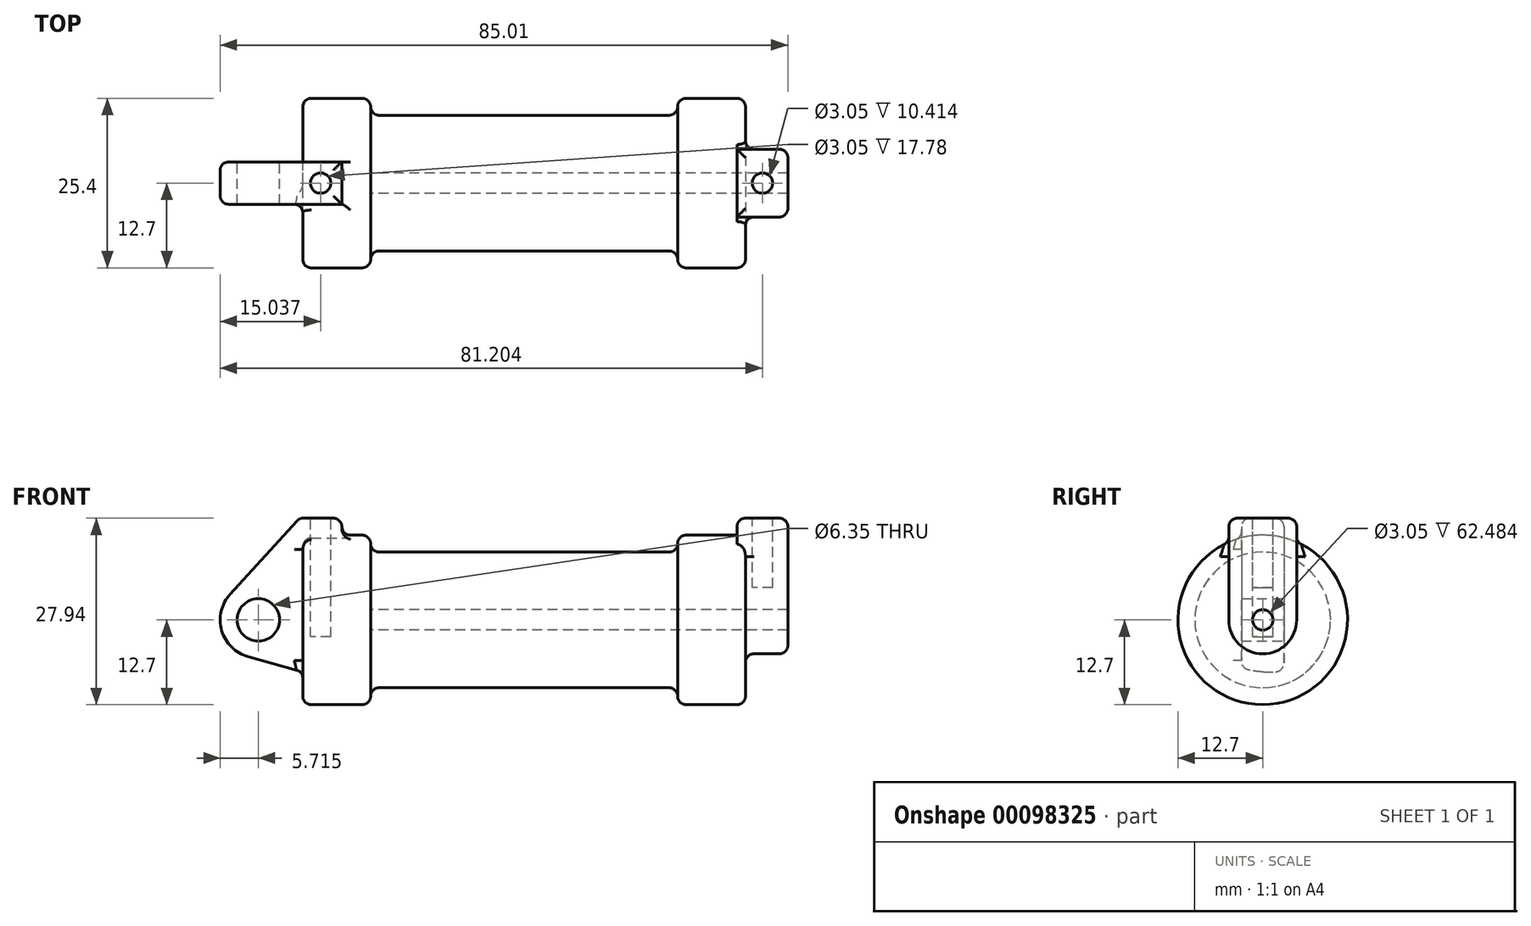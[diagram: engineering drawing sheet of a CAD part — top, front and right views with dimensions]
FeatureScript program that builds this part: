
annotation { "Feature Type Name" : "Feature", "Feature Type Description" : "" }
export const myFeature = defineFeature(function(context is Context, id is Id, definition is map)
    precondition{}
    {
        {
            var Q0;
            Q0=qCreatedBy(makeId("Front.planeOp"),FACE);
            var sketch = newSketch(context, id + "F0", { "sketchPlane" : qUnion([Q0])});
            skLineSegment(sketch, "E0", {"start": v(0, 0) * mm, "end": v(0, 12.7) * mm});
            skLineSegment(sketch, "E1", {"start": v(0, 12.7) * mm, "end": v(10.16, 12.7) * mm});
            skLineSegment(sketch, "E2", {"start": v(10.16, 12.7) * mm, "end": v(10.16, 10.16) * mm});
            skLineSegment(sketch, "E3", {"start": v(10.16, 10.16) * mm, "end": v(56.13, 10.16) * mm});
            skLineSegment(sketch, "E4", {"start": v(56.13, 10.16) * mm, "end": v(56.13, 12.7) * mm});
            skLineSegment(sketch, "E5", {"start": v(56.13, 12.7) * mm, "end": v(66.3, 12.7) * mm});
            skLineSegment(sketch, "E6", {"start": v(66.3, 12.7) * mm, "end": v(66.3, 0) * mm});
            skLineSegment(sketch, "E7", {"start": v(66.3, 0) * mm, "end": v(0, 0) * mm});
            skLineSegment(sketch, "E8", {"start": v(5.84, 15.24) * mm, "end": v(-0.5, 15.24) * mm});
            skLineSegment(sketch, "E9", {"start": v(-0.5, 15.24) * mm, "end": v(-10.88, 3.85) * mm});
            skLineSegment(sketch, "E10", {"start": v(0, 0) * mm, "end": v(-6.65, 0) * mm});
            skCircle(sketch, "E11", {"center": v(-6.65, 0) * mm, "radius": 5.72 * mm});
            skCircle(sketch, "E12", {"center": v(-6.65, 0) * mm, "radius": 3.18 * mm});
            skLineSegment(sketch, "E13", {"start": v(5.84, 15.24) * mm, "end": v(5.84, -9.4) * mm});
            skLineSegment(sketch, "E14", {"start": v(5.84, -9.4) * mm, "end": v(-8.18, -5.5) * mm});
            skSolve(sketch);
        }
        {
            var Q0;
            {var subQ0=sQuery(id+"F0.wireOp",EDGE,"E2");Q0=makeQuery(id+"F0.imprint","IMPRINT",FACE,{"disambiguationData":[TD([[makeQuery(id+"F0.imprint","IMPRINT",EDGE,{"derivedFrom":subQ0}),-1.0]])]});}
            var Q1;
            {var subQ0=sQuery(id+"F0.wireOp",EDGE,"E0");Q1=makeQuery(id+"F0.imprint","IMPRINT",FACE,{"disambiguationData":[TD([[makeQuery(id+"F0.imprint","IMPRINT",EDGE,{"derivedFrom":subQ0}),-1.0]])]});}
            var Q2;
            Q2=sQuery(id+"F0.wireOp",EDGE,"E10");
            revolve(context, id + "F1", {"entities" : qUnion([Q0, Q1]), "axis" : qUnion([Q2]), "revolveType" : RevolveType.FULL});
        }
        {
            var Q0;
            {var subQ3=sQuery(id+"F0.wireOp",EDGE,"E0");Q0=makeQuery(id+"F0.imprint","IMPRINT",FACE,{"disambiguationData":[TD([[makeQuery(id+"F0.imprint","IMPRINT",EDGE,{"derivedFrom":subQ3}),1.0]])]});}
            var Q1;
            {var subQ0=sQuery(id+"F0.wireOp",EDGE,"E14");Q1=makeQuery(id+"F0.imprint","IMPRINT",FACE,{"disambiguationData":[TD([[makeQuery(id+"F0.imprint","IMPRINT",EDGE,{"derivedFrom":subQ0}),-1.0]])]});}
            var Q2;
            {var subQ4=sQuery(id+"F0.wireOp",EDGE,"E12");Q2=makeQuery(id+"F0.imprint","IMPRINT",FACE,{"disambiguationData":[TD([[makeQuery(id+"F0.imprint","IMPRINT",EDGE,{"derivedFrom":subQ4}),-1.0]])]});}
            var Q3;
            {var subQ0=sQuery(id+"F0.wireOp",EDGE,"E0");Q3=makeQuery(id+"F0.imprint","IMPRINT",FACE,{"disambiguationData":[TD([[makeQuery(id+"F0.imprint","IMPRINT",EDGE,{"derivedFrom":subQ0}),-1.0]])]});}
            extrude(context, id + "F2", {"entities" : qUnion([Q0, Q1, Q2, Q3]), "operationType" : NewBodyOperationType.ADD, "endBound" : BoundingType.SYMMETRIC, "depth" : 6.35 * mm});
        }
        {
            var Q0;
            Q0=makeQuery(id+"F1.opRevolve","SWEPT_FACE",FACE,{"disambiguationData":[OSD([sQuery(id+"F0.wireOp",EDGE,"E6")])]});
            var sketch = newSketch(context, id + "F3", { "sketchPlane" : qUnion([Q0])});
            skCircle(sketch, "E15", {"center": v(0, 0) * mm, "radius": 1.52 * mm});
            skCircle(sketch, "E16", {"center": v(0, 0) * mm, "radius": 5.08 * mm});
            skLineSegment(sketch, "E17", {"start": v(5.08, 0) * mm, "end": v(5.08, 15.24) * mm});
            skLineSegment(sketch, "E18", {"start": v(5.08, 15.24) * mm, "end": v(-5.08, 15.24) * mm});
            skLineSegment(sketch, "E19", {"start": v(-5.08, 15.24) * mm, "end": v(-5.08, 0) * mm});
            skSolve(sketch);
        }
        {
            var Q0;
            Q0=makeQuery(id+"F3.imprint","IMPRINT",FACE,{"disambiguationData":[TD([[makeQuery(id+"F3.imprint","IMPRINT",EDGE,{"derivedFrom":sQuery(id+"F3.wireOp",EDGE,"E15")}),-1.0]])]});
            var Q1;
            {var subQ0=sQuery(id+"F3.wireOp",EDGE,"E17");var subQ1=sQuery(id+"F3.wireOp",EDGE,"E16");var subQ2=makeQuery(id+"F3.imprint","INTERSECT",VERTEX,{"derivedFrom":[subQ1,subQ0]});Q1=makeQuery(id+"F3.imprint","IMPRINT",FACE,{"disambiguationData":[TD([[makeQuery(id+"F3.imprint","IMPRINT",EDGE,{"disambiguationData":[TD([[subQ2,-1.0]])],"derivedFrom":subQ1}),-1.0]])]});}
            var Q2;
            {var subQ0=sQuery(id+"F3.wireOp",EDGE,"E18");Q2=makeQuery(id+"F3.imprint","IMPRINT",FACE,{"disambiguationData":[TD([[makeQuery(id+"F3.imprint","IMPRINT",EDGE,{"derivedFrom":subQ0}),1.0]])]});}
            extrude(context, id + "F4", {"entities" : qUnion([Q0, Q1, Q2]), "operationType" : NewBodyOperationType.ADD, "depth" : 6.35 * mm});
        }
        {
            var Q0;
            {var subQ0=sQuery(id+"F3.wireOp",EDGE,"E18");Q0=makeQuery(id+"F3.imprint","IMPRINT",FACE,{"disambiguationData":[TD([[makeQuery(id+"F3.imprint","IMPRINT",EDGE,{"derivedFrom":subQ0}),1.0]])]});}
            var Q1;
            Q1=makeQuery(id+"F3.imprint","IMPRINT",FACE,{"disambiguationData":[TD([[makeQuery(id+"F3.imprint","IMPRINT",EDGE,{"derivedFrom":sQuery(id+"F3.wireOp",EDGE,"E15")}),1.0]])]});
            extrude(context, id + "F5", {"entities" : qUnion([Q0, Q1]), "operationType" : NewBodyOperationType.ADD, "oppositeDirection" : true, "depth" : 1.27 * mm});
        }
        {
            var Q0;
            Q0=makeQuery(id+"F3.imprint","IMPRINT",FACE,{"disambiguationData":[TD([[makeQuery(id+"F3.imprint","IMPRINT",EDGE,{"derivedFrom":sQuery(id+"F3.wireOp",EDGE,"E15")}),1.0]])]});
            var Q1;
            Q1=makeQuery(id+"F1.opRevolve","SWEPT_FACE",FACE,{"disambiguationData":[OSD([sQuery(id+"F0.wireOp",EDGE,"E2")])]});
            extrude(context, id + "F6", {"entities" : qUnion([Q0]), "operationType" : NewBodyOperationType.REMOVE, "endBound" : BoundingType.UP_TO_SURFACE, "oppositeDirection" : true, "endBoundEntityFace" : qUnion([Q1]), "depth" : 25.4 * mm});
        }
        {
            var Q0;
            {var subQ0=sQuery(id+"F3.wireOp",EDGE,"E18");Q0=makeQuery(id+"F5.boolean.opBoolean","MERGE",FACE,{"derivedFrom":[makeQuery(id+"F4.opExtrude","SWEPT_FACE",FACE,{"disambiguationData":[OSD([subQ0])]}),makeQuery(id+"F5.opExtrude","SWEPT_FACE",FACE,{"disambiguationData":[OSD([subQ0])]})]});}
            var sketch = newSketch(context, id + "F7", { "sketchPlane" : qUnion([Q0])});
            skCircle(sketch, "E20", {"center": v(2.67, 0) * mm, "radius": 1.52 * mm});
            skLineSegment(sketch, "E21", {"start": v(-0.5, 0) * mm, "end": v(5.84, 0) * mm, "construction": true});
            skLineSegment(sketch, "E22", {"start": v(65.02, 0) * mm, "end": v(72.64, 0) * mm, "construction": true});
            skCircle(sketch, "E23", {"center": v(68.83, 0) * mm, "radius": 1.52 * mm});
            skSolve(sketch);
        }
        {
            var Q0;
            Q0=makeQuery(id+"F7.imprint","IMPRINT",FACE,{"disambiguationData":[TD([[makeQuery(id+"F7.imprint","IMPRINT",EDGE,{"derivedFrom":sQuery(id+"F7.wireOp",EDGE,"E23")}),1.0]])]});
            extrude(context, id + "F8", {"entities" : qUnion([Q0]), "operationType" : NewBodyOperationType.REMOVE, "oppositeDirection" : true, "depth" : 10.4 * mm});
        }
        {
            var Q0;
            Q0=makeQuery(id+"F7.imprint","IMPRINT",FACE,{"disambiguationData":[TD([[makeQuery(id+"F7.imprint","IMPRINT",EDGE,{"derivedFrom":sQuery(id+"F7.wireOp",EDGE,"E20")}),1.0]])]});
            extrude(context, id + "F9", {"entities" : qUnion([Q0]), "operationType" : NewBodyOperationType.REMOVE, "oppositeDirection" : true, "depth" : 17.78 * mm});
        }
        {
            var Q0;
            Q0=makeQuery(id+"F1.opRevolve","SWEPT_EDGE",EDGE,{"disambiguationData":[OSD([sQuery(id+"F0.wireOp",EDGE,"E1"),sQuery(id+"F0.wireOp",EDGE,"E2")])]});
            var Q1;
            Q1=makeQuery(id+"F1.opRevolve","SWEPT_EDGE",EDGE,{"disambiguationData":[OSD([sQuery(id+"F0.wireOp",EDGE,"E2"),sQuery(id+"F0.wireOp",EDGE,"E3")])]});
            var Q2;
            Q2=makeQuery(id+"F1.opRevolve","SWEPT_EDGE",EDGE,{"disambiguationData":[OSD([sQuery(id+"F0.wireOp",EDGE,"E4"),sQuery(id+"F0.wireOp",EDGE,"E5")])]});
            var Q3;
            Q3=makeQuery(id+"F4.boolean.opBoolean","SPLIT",EDGE,{"disambiguationData":[OD(1.0)],"derivedFrom":makeQuery(id+"F1.opRevolve","SWEPT_EDGE",EDGE,{"disambiguationData":[OSD([sQuery(id+"F0.wireOp",EDGE,"E5"),sQuery(id+"F0.wireOp",EDGE,"E6")])]})});
            var Q4;
            Q4=makeQuery(id+"F1.opRevolve","SWEPT_EDGE",EDGE,{"disambiguationData":[OSD([sQuery(id+"F0.wireOp",EDGE,"E0"),sQuery(id+"F0.wireOp",EDGE,"E1")])]});
            var Q5;
            Q5=makeQuery(id+"F1.opRevolve","SWEPT_EDGE",EDGE,{"disambiguationData":[OSD([sQuery(id+"F0.wireOp",EDGE,"E3"),sQuery(id+"F0.wireOp",EDGE,"E4")])]});
            fillet(context, id + "F10", {"entities" : qUnion([Q0, Q1, Q2, Q3, Q4, Q5]), "radius" : 1.27 * mm, "tangentPropagation" : true, "allowEdgeOverflow" : false});
        }
        {
            var Q0;
            Q0=makeQuery(id+"F2.opExtrude","CAP_EDGE",EDGE,{"disambiguationData":[OSD([sQuery(id+"F0.wireOp",EDGE,"E8")])],"isStart":false});
            var Q1;
            Q1=makeQuery(id+"F2.opExtrude","SWEPT_EDGE",EDGE,{"disambiguationData":[OSD([sQuery(id+"F0.wireOp",EDGE,"E8"),sQuery(id+"F0.wireOp",EDGE,"E13")])]});
            var Q2;
            Q2=makeQuery(id+"F2.opExtrude","CAP_EDGE",EDGE,{"disambiguationData":[OSD([sQuery(id+"F0.wireOp",EDGE,"E8")])],"isStart":true});
            var Q3;
            Q3=makeQuery(id+"F2.opExtrude","SWEPT_EDGE",EDGE,{"disambiguationData":[OSD([sQuery(id+"F0.wireOp",EDGE,"E8"),sQuery(id+"F0.wireOp",EDGE,"E9")])]});
            var Q4;
            Q4=makeQuery(id+"F2.opExtrude","CAP_EDGE",EDGE,{"disambiguationData":[OSD([sQuery(id+"F0.wireOp",EDGE,"E9")])],"isStart":true});
            var Q5;
            Q5=makeQuery(id+"F2.opExtrude","CAP_EDGE",EDGE,{"disambiguationData":[OSD([sQuery(id+"F0.wireOp",EDGE,"E9")])],"isStart":false});
            var Q6;
            Q6=makeQuery(id+"F2.boolean.opBoolean","INTERSECT",EDGE,{"derivedFrom":[makeQuery(id+"F1.opRevolve","SWEPT_FACE",FACE,{"disambiguationData":[OSD([sQuery(id+"F0.wireOp",EDGE,"E1")])]}),makeQuery(id+"F2.opExtrude","CAP_FACE",FACE,{"disambiguationData":[OSD([sQuery(id+"F0.wireOp",EDGE,"E8"),sQuery(id+"F0.wireOp",EDGE,"E9"),sQuery(id+"F0.wireOp",EDGE,"E11"),sQuery(id+"F0.wireOp",EDGE,"E12"),sQuery(id+"F0.wireOp",EDGE,"E13"),sQuery(id+"F0.wireOp",EDGE,"E14")])],"isStart":false})]});
            var Q7;
            Q7=makeQuery(id+"F2.boolean.opBoolean","INTERSECT",EDGE,{"derivedFrom":[makeQuery(id+"F1.opRevolve","SWEPT_FACE",FACE,{"disambiguationData":[OSD([sQuery(id+"F0.wireOp",EDGE,"E1")])]}),makeQuery(id+"F2.opExtrude","SWEPT_FACE",FACE,{"disambiguationData":[OSD([sQuery(id+"F0.wireOp",EDGE,"E13")])]})]});
            fillet(context, id + "F11", {"entities" : qUnion([Q0, Q1, Q2, Q3, Q4, Q5, Q6, Q7]), "radius" : 1.27 * mm, "tangentPropagation" : true, "allowEdgeOverflow" : false});
        }
        {
            var Q0;
            {var subQ0=sQuery(id+"F3.wireOp",EDGE,"E19");var subQ1=sQuery(id+"F3.wireOp",EDGE,"E18");Q0=makeQuery(id+"F5.boolean.opBoolean","MERGE",EDGE,{"derivedFrom":[makeQuery(id+"F4.opExtrude","SWEPT_EDGE",EDGE,{"disambiguationData":[OSD([subQ1,subQ0])]}),makeQuery(id+"F5.opExtrude","SWEPT_EDGE",EDGE,{"disambiguationData":[OSD([subQ1,subQ0])]})]});}
            var Q1;
            Q1=makeQuery(id+"F4.opExtrude","CAP_EDGE",EDGE,{"disambiguationData":[OSD([sQuery(id+"F3.wireOp",EDGE,"E18")])],"isStart":false});
            var Q2;
            {var subQ0=sQuery(id+"F3.wireOp",EDGE,"E18");var subQ1=sQuery(id+"F3.wireOp",EDGE,"E17");Q2=makeQuery(id+"F5.boolean.opBoolean","MERGE",EDGE,{"derivedFrom":[makeQuery(id+"F4.opExtrude","SWEPT_EDGE",EDGE,{"disambiguationData":[OSD([subQ1,subQ0])]}),makeQuery(id+"F5.opExtrude","SWEPT_EDGE",EDGE,{"disambiguationData":[OSD([subQ1,subQ0])]})]});}
            var Q3;
            Q3=makeQuery(id+"F5.opExtrude","CAP_EDGE",EDGE,{"disambiguationData":[OSD([sQuery(id+"F3.wireOp",EDGE,"E18")])],"isStart":false});
            var Q4;
            {var subQ0=sQuery(id+"F3.wireOp",EDGE,"E19");var subQ1=sQuery(id+"F3.wireOp",EDGE,"E16");Q4=makeQuery(id+"F4.boolean.opBoolean","SPLIT",EDGE,{"disambiguationData":[TD([makeQuery(id+"F4.opExtrude","SWEPT_FACE",FACE,{"disambiguationData":[OSD([subQ1])]})])],"derivedFrom":makeQuery(id+"F4.opExtrude","CAP_EDGE",EDGE,{"disambiguationData":[OSD([subQ0])],"isStart":true})});}
            var Q5;
            Q5=makeQuery(id+"F5.opExtrude","CAP_EDGE",EDGE,{"disambiguationData":[OSD([sQuery(id+"F0.wireOp",EDGE,"E5"),sQuery(id+"F0.wireOp",EDGE,"E6")])],"isStart":false});
            var Q6;
            Q6=makeQuery(id+"F4.opExtrude","CAP_EDGE",EDGE,{"disambiguationData":[OSD([sQuery(id+"F3.wireOp",EDGE,"E17")])],"isStart":false});
            fillet(context, id + "F12", {"entities" : qUnion([Q0, Q1, Q2, Q3, Q4, Q5, Q6]), "radius" : 1.27 * mm, "tangentPropagation" : true, "allowEdgeOverflow" : false});
        }
    });
